# Revit family: Noble Boiler NKB080N-150N
name_source: partatom
category: Mechanical Equipment
revit_build: Autodesk Revit 2016 (Build: 20151007_0715(x64)
units: mm (PartAtom-declared; Revit-internal decimal feet)

## family parameters
Always vertical = Yes
Cut with Voids When Loaded = No
Part Type = Normal
Room Calculation Point = No
Round Connector Dimension = Use Diameter
Shared = No
Work Plane-Based = No

## types (3) — shared parameters
# of Electrical Connections = 1
A_UNIT HEIGHT = 24"
BOILER WATER CONN = 1"
B_UNIT WIDTH = 17 1/4"
Bottom Clearance = 24"
Clearance Display = Yes
Condensate Diameter = 3/4"
Description = Noble Fire Tube Boiler
Electrical Offset from Right = 3"
FUEL TYPE = NATURAL GAS
Front Clearance = 24"
Front Clearance Depth = 24"
Fuel Type = Natural or LP
GAS CONN = 1/2"
Left Clearance = 12"
Manufacturer = Lochinvar
Right Clearance = 12"
SES BIM Studio # = 18 0649 05
Top Clearance = 6"
URL = http://www.lochinvar.com
Voltage/Heater = 120

## per-type parameters (varying)
| type | AIR INLET | C_UNIT DEPTH | D Vent Offset from Right | E Vent Offset from Back | Electrical Offset from Back | G Combustion Air Offset from Back | I Combustion Air Offset from Right | INPUT RATE (BTUH) | J Gas Offset from Left | K Gas Offset from Back | L Condensate Offset from Back | M Boiler Water Out Offset from Back | N Boiler Water In Offset from Back | O Boiler Water Offset from Right | OUTPUT RATE (BTUH) | P Condensate Offset from Right | VENT SIZE |
| NKB080N | 2" | 17 1/4" | 2 1/4" | 2 3/4" | 12 1/4" | 11" | 1 1/2" | 80,000 | 6 3/8" | 12 5/8" | 5 1/8" | 4 5/8" | 8 1/2" | 1 1/2" | 74,000 | 2 1/2" | 2" |
| NKB110N | 3" | 18" | 2 3/4" | 2 7/8" | 13" | 11 3/4" | 2 7/8" | 110,000 | 7 3/4" | 13 1/8" | 2 7/8" | 5 1/2" | 9" | 2" | 102,000 | 3" | 3" |
| NKB150N | 3" | 18" | 4 1/2" | 2 3/4" | 13" | 11 3/4" | 4 1/2" | 150,000 | 2 7/8" | 13 1/8" | 3" | 5 3/8" | 9 1/8" | 1 7/8" | 139,000 | 4 5/8" | 3" |

note: column(s) folded — value = type name in every type: MODEL NO., Model

## geometry (parser evidence)
native form markers: Sweep x2
no freeform markers — native parametric forms only
